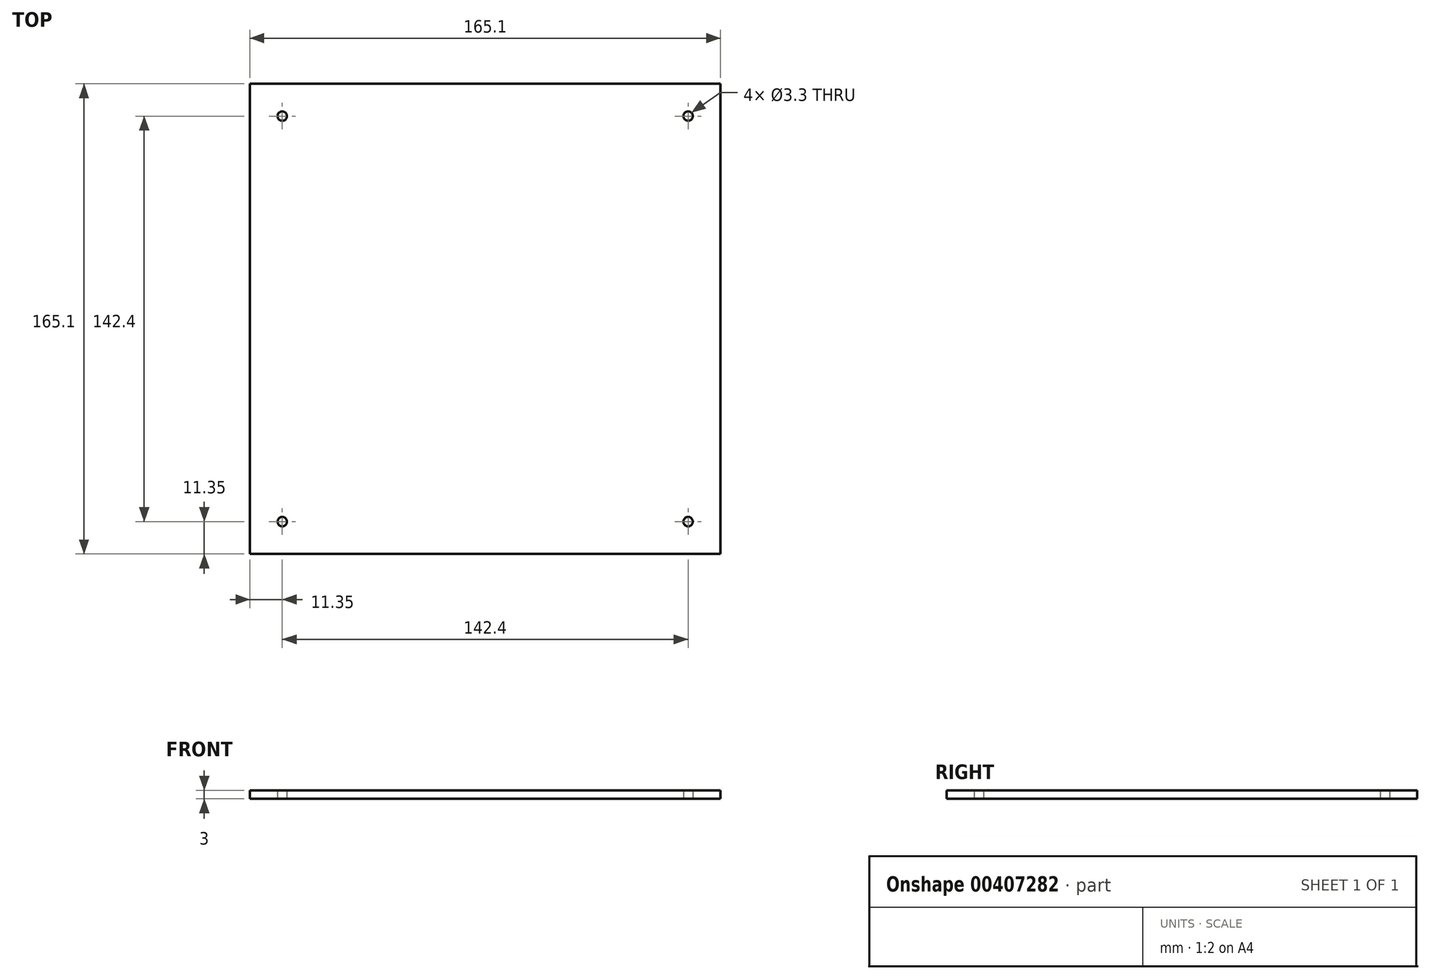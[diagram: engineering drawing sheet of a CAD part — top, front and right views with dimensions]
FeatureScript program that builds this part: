
annotation { "Feature Type Name" : "Feature", "Feature Type Description" : "" }
export const myFeature = defineFeature(function(context is Context, id is Id, definition is map)
    precondition{}
    {
        {
            var Q0;
            Q0=qCreatedBy(makeId("Top.planeOp"),FACE);
            var sketch = newSketch(context, id + "F0", { "sketchPlane" : qUnion([Q0])});
            skLineSegment(sketch, "E0.bottom", {"start": v(82.55, 82.55) * mm, "end": v(-82.55, 82.55) * mm});
            skLineSegment(sketch, "E0.top", {"start": v(82.55, -82.55) * mm, "end": v(-82.55, -82.55) * mm});
            skLineSegment(sketch, "E0.left", {"start": v(82.55, 82.55) * mm, "end": v(82.55, -82.55) * mm});
            skLineSegment(sketch, "E0.right", {"start": v(-82.55, 82.55) * mm, "end": v(-82.55, -82.55) * mm});
            skPoint(sketch, "E0.middle", {"position": v(0, 0) * mm});
            skLineSegment(sketch, "E1.bottom", {"start": v(71.2, 71.2) * mm, "end": v(-71.2, 71.2) * mm, "construction": true});
            skLineSegment(sketch, "E1.top", {"start": v(71.2, -71.2) * mm, "end": v(-71.2, -71.2) * mm, "construction": true});
            skLineSegment(sketch, "E1.left", {"start": v(71.2, 71.2) * mm, "end": v(71.2, -71.2) * mm, "construction": true});
            skLineSegment(sketch, "E1.right", {"start": v(-71.2, 71.2) * mm, "end": v(-71.2, -71.2) * mm, "construction": true});
            skSolve(sketch);
        }
        {
            var Q0;
            Q0 = qSketchRegion(id + "F0", true);
            extrude(context, id + "F1", {"entities" : qUnion([Q0]), "depth" : 3 * mm});
        }
        {
            var Q0;
            Q0=sQuery(id+"F0.wireOp",VERTEX,"E1.right.start");
            var Q1;
            Q1=sQuery(id+"F0.wireOp",VERTEX,"E1.left.start");
            var Q2;
            Q2=sQuery(id+"F0.wireOp",VERTEX,"E1.left.end");
            var Q3;
            Q3=sQuery(id+"F0.wireOp",VERTEX,"E1.right.end");
            var Q4;
            Q4=makeQuery(id+"F1.opExtrude","SWEPT_BODY",BODY,{"disambiguationData":[OSD([sQuery(id+"F0.wireOp",EDGE,"E0.bottom"),sQuery(id+"F0.wireOp",EDGE,"E0.top"),sQuery(id+"F0.wireOp",EDGE,"E0.left"),sQuery(id+"F0.wireOp",EDGE,"E0.right")])]});
            hole(context, id + "F2", {"style" : HoleStyle.SIMPLE, "endStyle" : HoleEndStyle.THROUGH, "oppositeDirection" : true, "standardTappedOrClearance" : lookupTablePath({ "standard" : "ISO", "fit" : "Normal", "size" : "M3", "type" : "Clearance" }), "standardBlindInLast" : lookupTablePath({ "fit" : "Standard", "standard" : "ISO", "size" : "M3", "type" : "Clearance" }), "holeDiameter" : 3.3 * mm, "isTappedThrough" : true, "tappedDepth" : 12 * mm, "tapClearance" : 3, "startFromSketch" : true, "locations" : qUnion([Q0, Q1, Q2, Q3]), "scope" : qUnion([Q4])});
        }
    });
